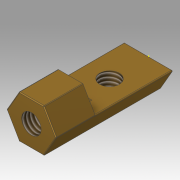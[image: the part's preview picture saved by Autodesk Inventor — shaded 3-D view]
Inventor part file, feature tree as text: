
AUTODESK INVENTOR PART (.ipt)
format: ipt  version: 2019.3 (Build 233278000, 278)  size: 166,912 bytes
history: native  units: mm
features: sketch x5, extrude x4, thread x2, fillet x2, projected_geometry x1
ambient origin geometry x8: Origin, YZ Plane, XZ Plane, XY Plane, X Axis, Y Axis, Z Axis, Center Point
bodies: Solid1 (feature_tree)
feature tree (14):
  sketch  "Sketch1"  dims[d0=5.5mm d1=15.0mm d2=0.0mm]
  extrude  "Extrusion1"  Depth=15.0mm TaperAngle=0.0deg
  extrude  "Extrusion2"  Depth=6.5mm TaperAngle=0.0deg
  thread  "Thread1"  [1 undecoded]
  extrude  "Extrusion3"  Depth=6.5mm TaperAngle=0.0deg
  extrude  "Extrusion4"  Depth=10.0mm
  thread  "Thread2"  [1 undecoded]
  fillet  "Fillet1"  Radius=10.0mm
  fillet  "Fillet2"  Radius=0.1mm
  sketch  "Sketch2"  dims[d3=2.5mm d4=6.5mm d5=0.0mm d6=10.0mm d7=0.0mm]
  sketch  "Sketch3"  dims[d8=5.0mm d9=6.5mm d10=0.0mm]
  projected_geometry  "Projected Loop1"
  sketch  "Sketch4"  dims[d11=2.5mm d12=10.0mm d13=6.5mm d14=0.0mm d15=10.0mm d16=0.0mm d17=0.1mm]
  sketch  "Sketch5"  dims[d18=0.1mm]
note: 2 required parameter values undecoded (feature->parameter linkage not recoverable at this tier; creation-order binding heuristic only, values carry confidence <= 0.55)
